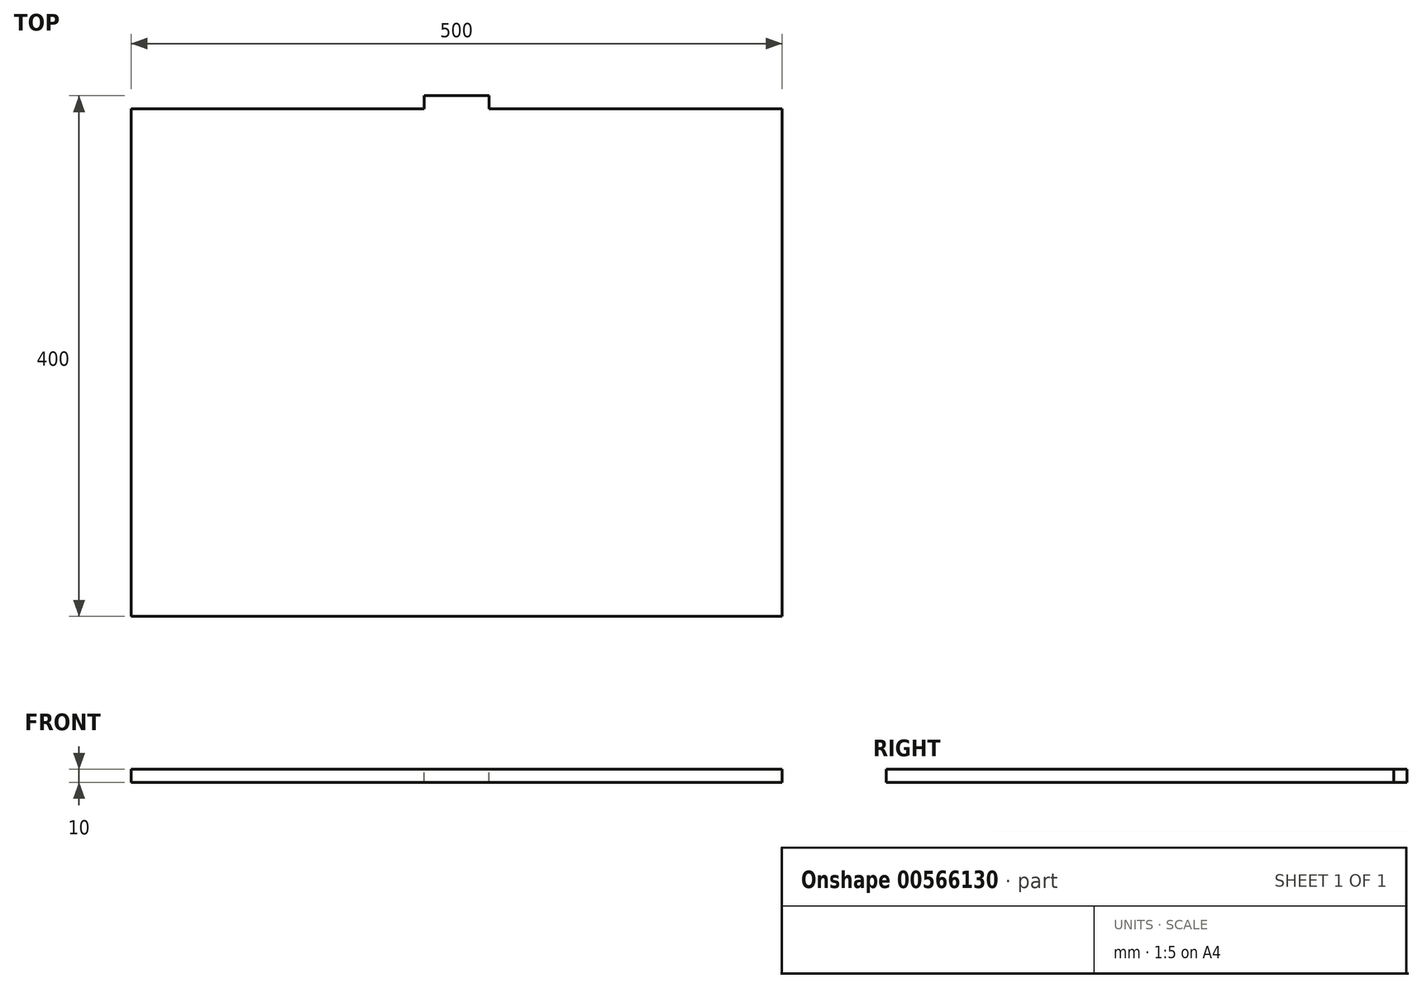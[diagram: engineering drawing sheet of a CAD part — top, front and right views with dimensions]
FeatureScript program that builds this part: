
annotation { "Feature Type Name" : "Feature", "Feature Type Description" : "" }
export const myFeature = defineFeature(function(context is Context, id is Id, definition is map)
    precondition{}
    {
        {
            var Q0;
            Q0=qCreatedBy(makeId("Front.planeOp"),FACE);
            var sketch = newSketch(context, id + "F0", { "sketchPlane" : qUnion([Q0])});
            skLineSegment(sketch, "E0.left", {"start": v(-250, 60) * mm, "end": v(-250, 50) * mm});
            skLineSegment(sketch, "E0.right", {"start": v(250, 60) * mm, "end": v(250, 50) * mm});
            skLineSegment(sketch, "E1", {"start": v(-250, 60) * mm, "end": v(250, 60) * mm});
            skLineSegment(sketch, "E2", {"start": v(250, 50) * mm, "end": v(-250, 50) * mm});
            skLineSegment(sketch, "E3", {"start": v(-250, 50) * mm, "end": v(-250, 60) * mm});
            skSolve(sketch);
        }
        {
            var Q0;
            Q0=makeQuery(id+"F0.imprint","IMPRINT",FACE,{"disambiguationData":[TD([[makeQuery(id+"F0.imprint","IMPRINT",EDGE,{"derivedFrom":sQuery(id+"F0.wireOp",EDGE,"E1")}),-1.0]])]});
            extrude(context, id + "F1", {"entities" : qUnion([Q0]), "depth" : 390 * mm, "offsetDistance" : 25 * mm});
        }
        {
            var Q0;
            Q0=makeQuery(id+"F1.opExtrude","CAP_FACE",FACE,{"disambiguationData":[OSD([sQuery(id+"F0.wireOp",EDGE,"E1"),sQuery(id+"F0.wireOp",EDGE,"E0.right"),sQuery(id+"F0.wireOp",EDGE,"E2"),sQuery(id+"F0.wireOp",EDGE,"E3")])],"isStart":true});
            var sketch = newSketch(context, id + "F2", { "sketchPlane" : qUnion([Q0])});
            skLineSegment(sketch, "E4", {"start": v(25, 50) * mm, "end": v(25, 60) * mm});
            skLineSegment(sketch, "E5", {"start": v(-25, 50) * mm, "end": v(-25, 60) * mm});
            skLineSegment(sketch, "E6", {"start": v(-25, 60) * mm, "end": v(25, 60) * mm});
            skLineSegment(sketch, "E7", {"start": v(25, 50) * mm, "end": v(-25, 50) * mm});
            skSolve(sketch);
        }
        {
            var Q0;
            Q0=makeQuery(id+"F2.imprint","IMPRINT",FACE,{"disambiguationData":[TD([[makeQuery(id+"F2.imprint","IMPRINT",EDGE,{"derivedFrom":sQuery(id+"F2.wireOp",EDGE,"E4")}),1.0]])]});
            extrude(context, id + "F3", {"entities" : qUnion([Q0]), "operationType" : NewBodyOperationType.ADD, "depth" : 10 * mm, "offsetDistance" : 25 * mm});
        }
    });
